# Revit family: PARLÉ TCM - Network Box_rev1
name_source: partatom
category: Communication Devices
units: mm (PartAtom-declared; Revit-internal decimal feet)

## family parameters
Cut with Voids When Loaded = No
Host = Face
Maintain Annotation Orientation = No
Part Type = Normal
Room Calculation Point = Yes
Round Connector Dimension = Use Diameter
Shared = Yes

## types (4) — shared parameters
Case Finish = Black Finish
Connector = Three RJ-45: one between TCM-X network box and switch, one between the network box and microphone, the other between TCM-X network box and TCM-XEX
Default Elevation = 0' - 0"
Depth = 0' - 5 3/16"
Dynamic Range = 92dB, A-Weighted
Height = 0' - 1 3/16"
Manufacturer = Biamp Systems
Manufacturer URL = https://www.biamp.com
Max Distance Between Devices = 33 feet (10 meters) between TCM-XEX and DSP host device
Power = PoE (IEEE 802.3at Class 3, 15.4W)
Product Documentation Link = https://downloads.biamp.com
Product Page URL = https://www.biamp.com
Regulatory Compliance = FCC Part 15B (USA) CE marked (Europe) UL and C-UL listed (USA and Canada) RoHS Directive (Europe) Evaluated to the requirements of UL 2043 and is suitable for use in air handling spaces
Weight Product = 1.4
Width = 0' - 6 13/16"

## per-type parameters (varying)
| type | Amplifier | Ceiling/Wall Mounting | Description | Model | POE Power | POE+ |
| PARLÉ™ TCM-X Network Box - Ceiling mounted |  | 180.00° | Ceiling microphone Network Box only. (Cost includes mic.) | Parlé TCM-X | 15.4 | No |
| PARLÉ™ TCM-XA Network Box - Ceiling mounted | 2X Class D, Single Channel Driven, (4Ω, 8Ω): 8W, Dual Channel Driven (4Ω, 8Ω): 4W | 180.00° | Ceiling microphone Network Box with amplifier only. (Cost includes mic.) | Parlé TCM-XA | 30 | Yes |
| PARLÉ™ TCM-X Network Box - Wall mounted |  | 0.00° | Ceiling microphone Network Box only. (Cost includes mic.) | Parlé TCM-X | 15.4 | No |
| PARLÉ™ TCM-XA Network Box - Wall mounted | 2X Class D, Single Channel Driven, (4Ω, 8Ω): 8W, Dual Channel Driven (4Ω, 8Ω): 4W | 0.00° | Ceiling microphone Network Box with amplifier only. (Cost includes mic.) | Parlé TCM-XA | 30 | Yes |

## geometry (parser evidence)
native form markers: Blend x4, Sweep x2
no freeform markers — native parametric forms only
